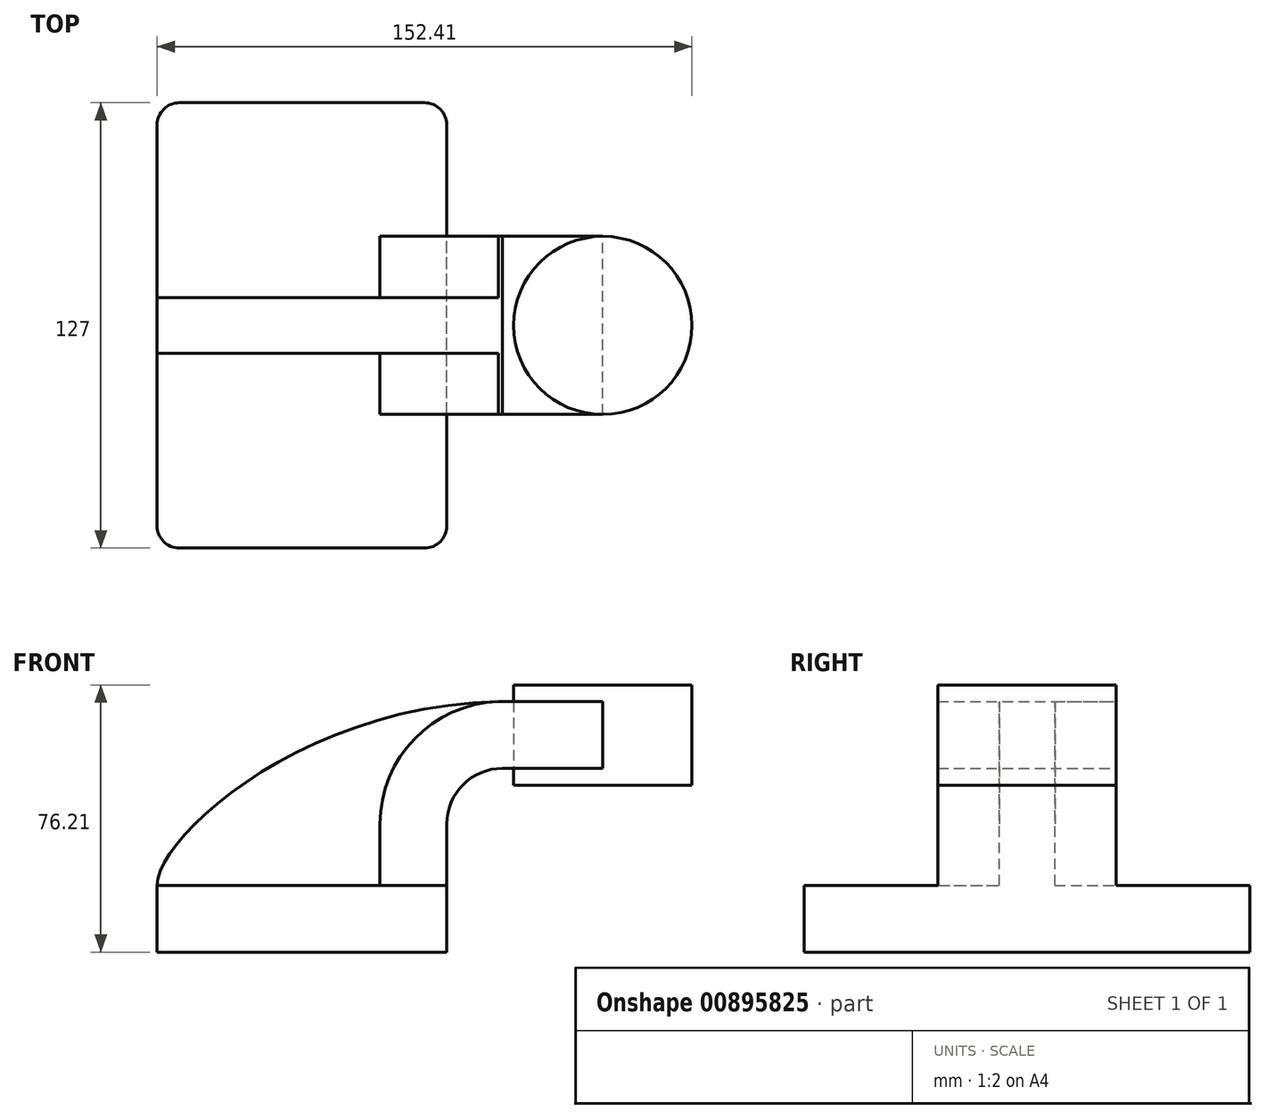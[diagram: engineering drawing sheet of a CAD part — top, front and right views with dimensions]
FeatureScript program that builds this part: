
annotation { "Feature Type Name" : "Feature", "Feature Type Description" : "" }
export const myFeature = defineFeature(function(context is Context, id is Id, definition is map)
    precondition{}
    {
        {
            var Q0;
            Q0=qCreatedBy(makeId("Front.planeOp"),FACE);
            var sketch = newSketch(context, id + "F0", { "sketchPlane" : qUnion([Q0])});
            skLineSegment(sketch, "E0.bottom", {"start": v(41.28, -9.52) * mm, "end": v(-41.27, -9.52) * mm});
            skLineSegment(sketch, "E0.top", {"start": v(41.27, 9.53) * mm, "end": v(-41.28, 9.53) * mm});
            skLineSegment(sketch, "E0.left", {"start": v(41.28, -9.52) * mm, "end": v(41.28, 9.53) * mm});
            skLineSegment(sketch, "E0.right", {"start": v(-41.27, -9.52) * mm, "end": v(-41.28, 9.53) * mm});
            skPoint(sketch, "E0.middle", {"position": v(0, 0) * mm});
            skLineSegment(sketch, "E1.bottom", {"start": v(111.12, 38.1) * mm, "end": v(60.33, 38.1) * mm});
            skLineSegment(sketch, "E1.top", {"start": v(111.12, 66.68) * mm, "end": v(60.32, 66.68) * mm});
            skLineSegment(sketch, "E1.left", {"start": v(111.13, 38.1) * mm, "end": v(111.13, 66.68) * mm});
            skLineSegment(sketch, "E1.right", {"start": v(60.33, 38.1) * mm, "end": v(60.32, 66.68) * mm});
            skPoint(sketch, "E1.middle", {"position": v(85.72, 52.39) * mm});
            skLineSegment(sketch, "E2", {"start": v(41.27, 9.53) * mm, "end": v(41.27, 27) * mm});
            skArc(sketch, "E3", {"start": v(41.27, 27) * mm, "mid": v(45.92, 38.23) * mm, "end": v(57.15, 42.88) * mm});
            skLineSegment(sketch, "E4", {"start": v(57.15, 42.88) * mm, "end": v(85.72, 42.88) * mm});
            skLineSegment(sketch, "E5.0", {"start": v(-250859.93, 9.53) * mm, "end": v(-250859.93, 27) * mm});
            skLineSegment(sketch, "E6.0", {"start": v(57.15, 61.93) * mm, "end": v(85.72, 61.93) * mm});
            skArc(sketch, "E6.1", {"start": v(22.23, 27) * mm, "mid": v(32.45, 51.7) * mm, "end": v(57.15, 61.93) * mm});
            skLineSegment(sketch, "E6.2", {"start": v(22.22, 9.53) * mm, "end": v(22.22, 27) * mm});
            skLineSegment(sketch, "E7", {"start": v(85.72, 38.1) * mm, "end": v(85.72, 66.68) * mm});
            skFitSpline(sketch, "E8", {"points": [v(-41.28, 9.53) * mm, v(57.15, 61.93) * mm], "startDerivative": vector(0, 40.74) * mm, "endDerivative": vector(171.45, 2) * mm});
            skPoint(sketch, "E9.1.internal.snap0", {"position": v(32.45, 51.7) * mm});
            skPoint(sketch, "E10", {"position": v(0, 9.53) * mm});
            skSolve(sketch);
        }
        {
            var Q0;
            Q0=makeQuery(id+"F0.imprint","IMPRINT",FACE,{"disambiguationData":[TD([[makeQuery(id+"F0.imprint","IMPRINT",EDGE,{"derivedFrom":sQuery(id+"F0.wireOp",EDGE,"E0.bottom")}),-1.0]])]});
            extrude(context, id + "F1", {"entities" : qUnion([Q0]), "endBound" : BoundingType.SYMMETRIC, "depth" : 127 * mm, "offsetDistance" : 25.4 * mm});
        }
        {
            var Q0;
            {var subQ1=sQuery(id+"F0.wireOp",EDGE,"E2");Q0=makeQuery(id+"F0.imprint","IMPRINT",FACE,{"disambiguationData":[TD([[makeQuery(id+"F0.imprint","IMPRINT",EDGE,{"derivedFrom":subQ1}),1.0]])]});}
            var Q1;
            {var subQ0=sQuery(id+"F0.wireOp",EDGE,"E4");var subQ1=sQuery(id+"F0.wireOp",EDGE,"E1.right");var subQ2=makeQuery(id+"F0.imprint","INTERSECT",VERTEX,{"derivedFrom":[subQ1,subQ0]});Q1=makeQuery(id+"F0.imprint","IMPRINT",FACE,{"disambiguationData":[TD([[makeQuery(id+"F0.imprint","IMPRINT",EDGE,{"disambiguationData":[TD([[subQ2,-1.0]])],"derivedFrom":subQ1}),-1.0]])]});}
            extrude(context, id + "F2", {"entities" : qUnion([Q0, Q1]), "operationType" : NewBodyOperationType.ADD, "endBound" : BoundingType.SYMMETRIC, "depth" : 50.8 * mm, "offsetDistance" : 25.4 * mm});
        }
        {
            var Q0;
            {var subQ3=sQuery(id+"F0.wireOp",EDGE,"E6.2");Q0=makeQuery(id+"F0.imprint","IMPRINT",FACE,{"disambiguationData":[TD([[makeQuery(id+"F0.imprint","IMPRINT",EDGE,{"derivedFrom":subQ3}),1.0]])]});}
            extrude(context, id + "F3", {"entities" : qUnion([Q0]), "operationType" : NewBodyOperationType.ADD, "endBound" : BoundingType.SYMMETRIC, "depth" : 15.88 * mm, "offsetDistance" : 25.4 * mm});
        }
        {
            var Q0;
            {var subQ0=sQuery(id+"F0.wireOp",EDGE,"E1.left");Q0=makeQuery(id+"F0.imprint","IMPRINT",FACE,{"disambiguationData":[TD([[makeQuery(id+"F0.imprint","IMPRINT",EDGE,{"derivedFrom":subQ0}),1.0]])]});}
            var Q1;
            Q1=sQuery(id+"F0.wireOp",EDGE,"E7");
            revolve(context, id + "F4", {"surfaceOperationType" : NewSurfaceOperationType.NEW, "entities" : qUnion([Q0]), "axis" : qUnion([Q1]), "revolveType" : RevolveType.FULL});
        }
        {
            var Q0;
            Q0=makeQuery(id+"F1.opExtrude","CAP_EDGE",EDGE,{"disambiguationData":[OSD([sQuery(id+"F0.wireOp",EDGE,"E0.left")])],"isStart":false});
            var Q1;
            Q1=makeQuery(id+"F1.opExtrude","CAP_EDGE",EDGE,{"disambiguationData":[OSD([sQuery(id+"F0.wireOp",EDGE,"E0.left")])],"isStart":true});
            var Q2;
            Q2=makeQuery(id+"F1.opExtrude","CAP_EDGE",EDGE,{"disambiguationData":[OSD([sQuery(id+"F0.wireOp",EDGE,"E0.right")])],"isStart":false});
            var Q3;
            Q3=makeQuery(id+"F1.opExtrude","CAP_EDGE",EDGE,{"disambiguationData":[OSD([sQuery(id+"F0.wireOp",EDGE,"E0.right")])],"isStart":true});
            fillet(context, id + "F5", {"entities" : qUnion([Q0, Q1, Q2, Q3]), "radius" : 6.35 * mm, "tangentPropagation" : true, "allowEdgeOverflow" : false});
        }
    });
